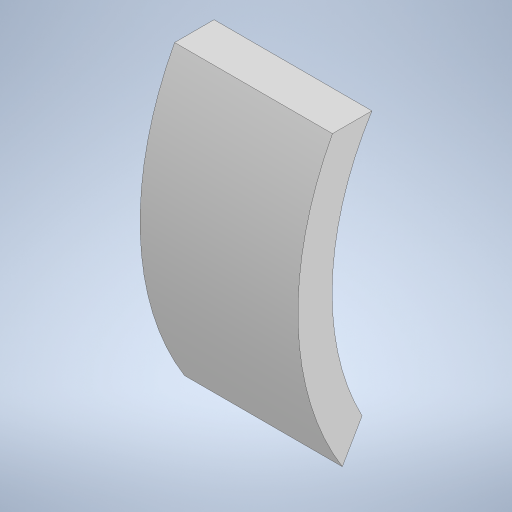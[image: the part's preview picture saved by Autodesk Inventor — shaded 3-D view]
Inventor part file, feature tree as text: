
AUTODESK INVENTOR PART (.ipt)
format: ipt  version: 2024 (Build 280153000, 153)  size: 221,696 bytes
history: native  units: in
note: dims shown in document units (in); Inventor stores cm internally (conversion verified against a paired STEP export)
features: sketch x2, sweep x1
ambient origin geometry x8: Origin, YZ Plane, XZ Plane, XY Plane, X Axis, Y Axis, Z Axis, Center Point
bodies: Solid1 (feature_tree)
feature tree (3):
  sweep  "Sweep1"
  sketch  "Sketch5"  dims[d4=0.1969in d5=2.7559in]
  sketch  "Sketch7"  dims[d6=180.0deg d7=2.7559in d13=1.5748in d14=0.3937in d15=0.0in d16=0.0in]
